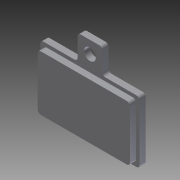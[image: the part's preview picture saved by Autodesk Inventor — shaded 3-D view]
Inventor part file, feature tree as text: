
AUTODESK INVENTOR PART (.ipt)
format: ipt  version: 2011 (Build 150239000, 239)  size: 120,320 bytes
history: native  units: in
note: dims shown in document units (in); Inventor stores cm internally (conversion verified against a paired STEP export)
features: sketch x4, extrude x3, hole x1, fillet x1
ambient origin geometry x8: Origin, YZ Plane, XZ Plane, XY Plane, X Axis, Y Axis, Z Axis, Center Point
bodies: Solid1 (feature_tree)
feature tree (9):
  extrude  "Extrusion1"  Depth=0.3937in
  extrude  "Extrusion2"  Depth=0.0222in
  extrude  "Extrusion3"  Depth=0.1575in
  hole  "Hole1"  [1 undecoded]
  fillet  "Fillet1"  Radius=0.0197in
  sketch  "Sketch1"  dims[d0=0.6299in d1=0.3937in]
  sketch  "Sketch2"  dims[d2=0.0787in d3=0.0in d4=0.0222in]
  sketch  "Sketch3"  dims[d5=0.0394in d6=0.0in d7=0.1575in]
  sketch  "Sketch4"  dims[d8=0.2362in d9=0.1575in d10=0.0in d11=0.075in d12=0.75in d13=0.375in d14=0.25in d15=0.5635in d16=1.0in d17=0.8108in d18=0.0197in]
note: 1 required parameter value undecoded (feature->parameter linkage not recoverable at this tier; creation-order binding heuristic only, values carry confidence <= 0.55)
